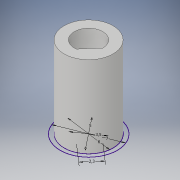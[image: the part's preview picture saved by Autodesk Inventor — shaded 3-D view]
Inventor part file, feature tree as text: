
AUTODESK INVENTOR PART (.ipt)
format: ipt  version: 2019 (Build 230136000, 136)  size: 105,472 bytes
history: native  units: mm
features: extrude x2, other x1, sketch x1
ambient origin geometry x8: Origin, YZ Plane, XZ Plane, XY Plane, X Axis, Y Axis, Z Axis, Center Point
bodies: Body1 (feature_tree)
feature tree (4):
  other  "Sólido1"
  sketch  "Boceto1"  dims[d0=3.5mm d1=2.3mm d2=7.0mm d3=10.0mm d4=0.0mm d5=6.0mm d6=10.0mm d7=0.0mm d8=5.0mm]
  extrude  "Extrusión1"  Depth=10.0mm
  extrude  "Extrusión2"  Depth=10.0mm
